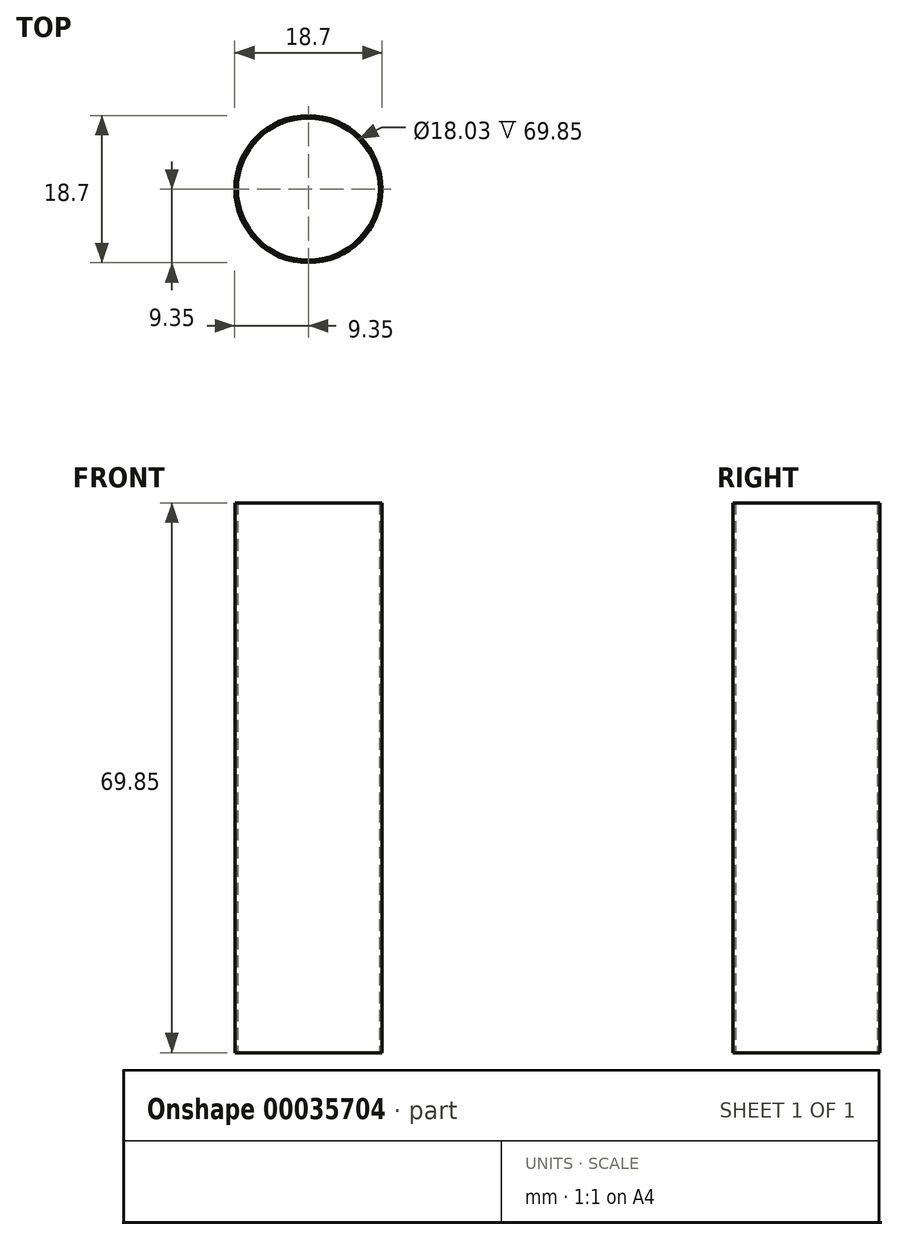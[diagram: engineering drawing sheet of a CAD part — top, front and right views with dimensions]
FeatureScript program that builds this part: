
annotation { "Feature Type Name" : "Feature", "Feature Type Description" : "" }
export const myFeature = defineFeature(function(context is Context, id is Id, definition is map)
    precondition{}
    {
        {
            var Q0;
            Q0=qCreatedBy(makeId("Front.planeOp"),FACE);
            var sketch = newSketch(context, id + "F0", { "sketchPlane" : qUnion([Q0])});
            skLineSegment(sketch, "E0", {"start": v(0, 0) * mm, "end": v(0, 69.85) * mm});
            skLineSegment(sketch, "E1", {"start": v(0, 69.85) * mm, "end": v(9.02, 69.85) * mm});
            skLineSegment(sketch, "E2", {"start": v(9.02, 69.85) * mm, "end": v(9.02, 0) * mm});
            skLineSegment(sketch, "E3", {"start": v(9.02, 0) * mm, "end": v(0, 0) * mm});
            skLineSegment(sketch, "E4", {"start": v(9.02, 0) * mm, "end": v(9.35, 0) * mm});
            skLineSegment(sketch, "E5", {"start": v(9.35, 0) * mm, "end": v(9.35, 69.85) * mm});
            skLineSegment(sketch, "E6", {"start": v(9.35, 69.85) * mm, "end": v(9.02, 69.85) * mm});
            skSolve(sketch);
        }
        {
            var Q0;
            Q0=makeQuery(id+"F0.imprint","IMPRINT",FACE,{"disambiguationData":[TD([[makeQuery(id+"F0.imprint","IMPRINT",EDGE,{"derivedFrom":sQuery(id+"F0.wireOp",EDGE,"E2")}),1.0]])]});
            var Q1;
            Q1=sQuery(id+"F0.wireOp",EDGE,"E0");
            revolve(context, id + "F1", {"entities" : qUnion([Q0]), "axis" : qUnion([Q1]), "revolveType" : RevolveType.FULL});
        }
    });
